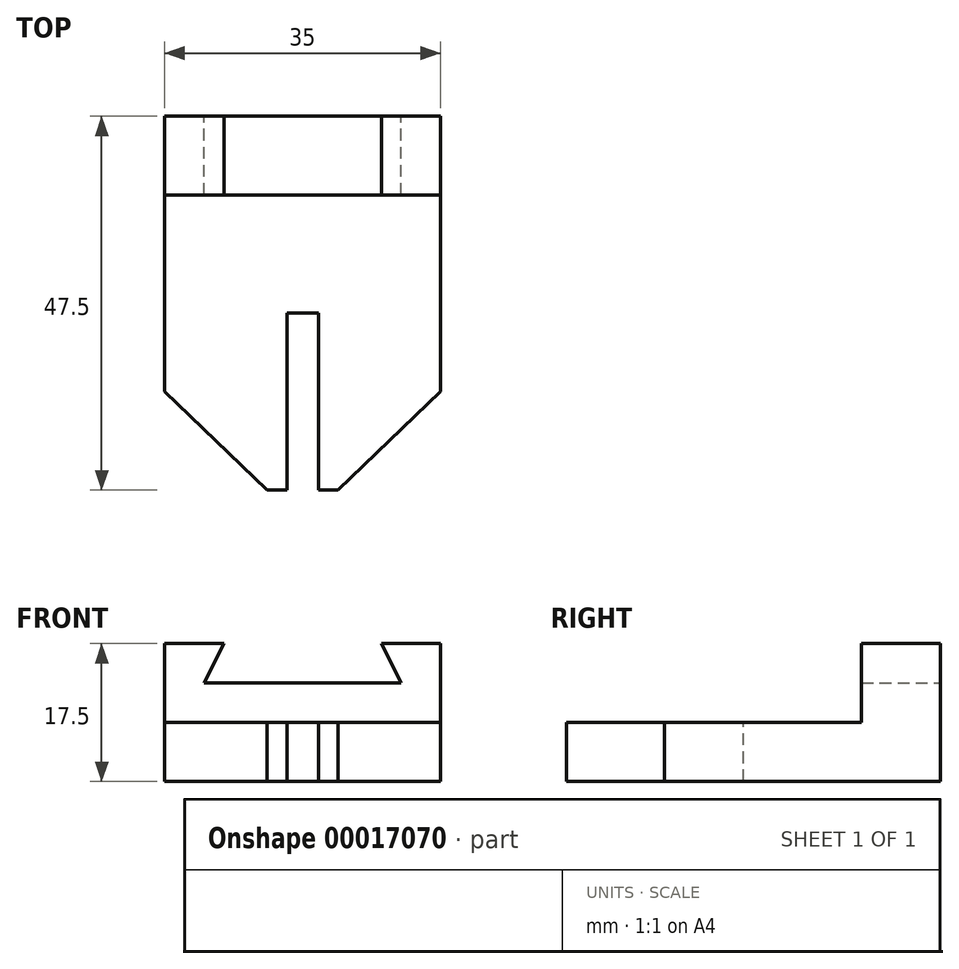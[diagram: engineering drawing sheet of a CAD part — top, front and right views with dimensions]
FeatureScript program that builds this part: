
annotation { "Feature Type Name" : "Feature", "Feature Type Description" : "" }
export const myFeature = defineFeature(function(context is Context, id is Id, definition is map)
    precondition{}
    {
        {
            var Q0;
            Q0=qCreatedBy(makeId("Front.planeOp"),FACE);
            var sketch = newSketch(context, id + "F0", { "sketchPlane" : qUnion([Q0])});
            skLineSegment(sketch, "E0", {"start": v(-13.37, 0.94) * mm, "end": v(-13.37, 18.44) * mm});
            skLineSegment(sketch, "E1", {"start": v(-13.37, 18.44) * mm, "end": v(-5.87, 18.44) * mm});
            skLineSegment(sketch, "E2", {"start": v(-5.87, 18.44) * mm, "end": v(-8.37, 13.44) * mm});
            skLineSegment(sketch, "E3", {"start": v(-8.37, 13.44) * mm, "end": v(16.63, 13.44) * mm});
            skLineSegment(sketch, "E4", {"start": v(16.63, 13.44) * mm, "end": v(14.13, 18.44) * mm});
            skLineSegment(sketch, "E5", {"start": v(14.13, 18.44) * mm, "end": v(21.63, 18.44) * mm});
            skLineSegment(sketch, "E6", {"start": v(21.63, 18.44) * mm, "end": v(21.63, 0.94) * mm});
            skLineSegment(sketch, "E7", {"start": v(21.63, 0.94) * mm, "end": v(-13.37, 0.94) * mm});
            skLineSegment(sketch, "E8", {"start": v(-13.37, 8.44) * mm, "end": v(21.63, 8.44) * mm});
            skSolve(sketch);
        }
        {
            var Q0;
            {var subQ1=sQuery(id+"F0.wireOp",EDGE,"E7");Q0=makeQuery(id+"F0.imprint","IMPRINT",FACE,{"disambiguationData":[TD([[makeQuery(id+"F0.imprint","IMPRINT",EDGE,{"derivedFrom":subQ1}),-1.0]])]});}
            extrude(context, id + "F1", {"entities" : qUnion([Q0]), "depth" : 47.5 * mm});
        }
        {
            var Q0;
            {var subQ3=sQuery(id+"F0.wireOp",EDGE,"E1");Q0=makeQuery(id+"F0.imprint","IMPRINT",FACE,{"disambiguationData":[TD([[makeQuery(id+"F0.imprint","IMPRINT",EDGE,{"derivedFrom":subQ3}),-1.0]])]});}
            extrude(context, id + "F2", {"entities" : qUnion([Q0]), "operationType" : NewBodyOperationType.ADD, "depth" : 10 * mm});
        }
        {
            var Q0;
            Q0=makeQuery(id+"F1.opExtrude","SWEPT_FACE",FACE,{"disambiguationData":[OSD([sQuery(id+"F0.wireOp",EDGE,"E8")])]});
            var sketch = newSketch(context, id + "F3", { "sketchPlane" : qUnion([Q0])});
            skLineSegment(sketch, "E9", {"start": v(-13.37, -35) * mm, "end": v(-0.37, -47.5) * mm});
            skLineSegment(sketch, "E10", {"start": v(21.63, -35) * mm, "end": v(8.63, -47.5) * mm});
            skLineSegment(sketch, "E11", {"start": v(8.63, -47.5) * mm, "end": v(21.63, -35) * mm});
            skLineSegment(sketch, "E12", {"start": v(8.63, -47.5) * mm, "end": v(21.63, -47.5) * mm});
            skLineSegment(sketch, "E13", {"start": v(21.63, -47.5) * mm, "end": v(21.63, -35) * mm});
            skLineSegment(sketch, "E14", {"start": v(-13.37, -47.5) * mm, "end": v(-0.37, -47.5) * mm});
            skLineSegment(sketch, "E15", {"start": v(-13.37, -47.5) * mm, "end": v(-13.37, -35) * mm});
            skLineSegment(sketch, "E16", {"start": v(2.13, -47.5) * mm, "end": v(2.13, -25) * mm});
            skLineSegment(sketch, "E17", {"start": v(2.13, -25) * mm, "end": v(6.13, -25) * mm});
            skLineSegment(sketch, "E18", {"start": v(6.13, -25) * mm, "end": v(6.13, -47.5) * mm});
            skLineSegment(sketch, "E19", {"start": v(-0.37, -47.5) * mm, "end": v(2.13, -47.5) * mm});
            skLineSegment(sketch, "E20", {"start": v(2.13, -47.5) * mm, "end": v(6.13, -47.5) * mm});
            skSolve(sketch);
        }
        {
            var Q0;
            Q0 = qSketchRegion(id + "F3", true);
            extrude(context, id + "F4", {"entities" : qUnion([Q0]), "operationType" : NewBodyOperationType.REMOVE, "endBound" : BoundingType.THROUGH_ALL, "oppositeDirection" : true, "depth" : 25 * mm});
        }
        {
            var Q0;
            Q0 = qSketchRegion(id + "F3", true);
            extrude(context, id + "F5", {"entities" : qUnion([Q0]), "operationType" : NewBodyOperationType.REMOVE, "endBound" : BoundingType.THROUGH_ALL, "oppositeDirection" : true, "depth" : 25 * mm});
        }
    });
